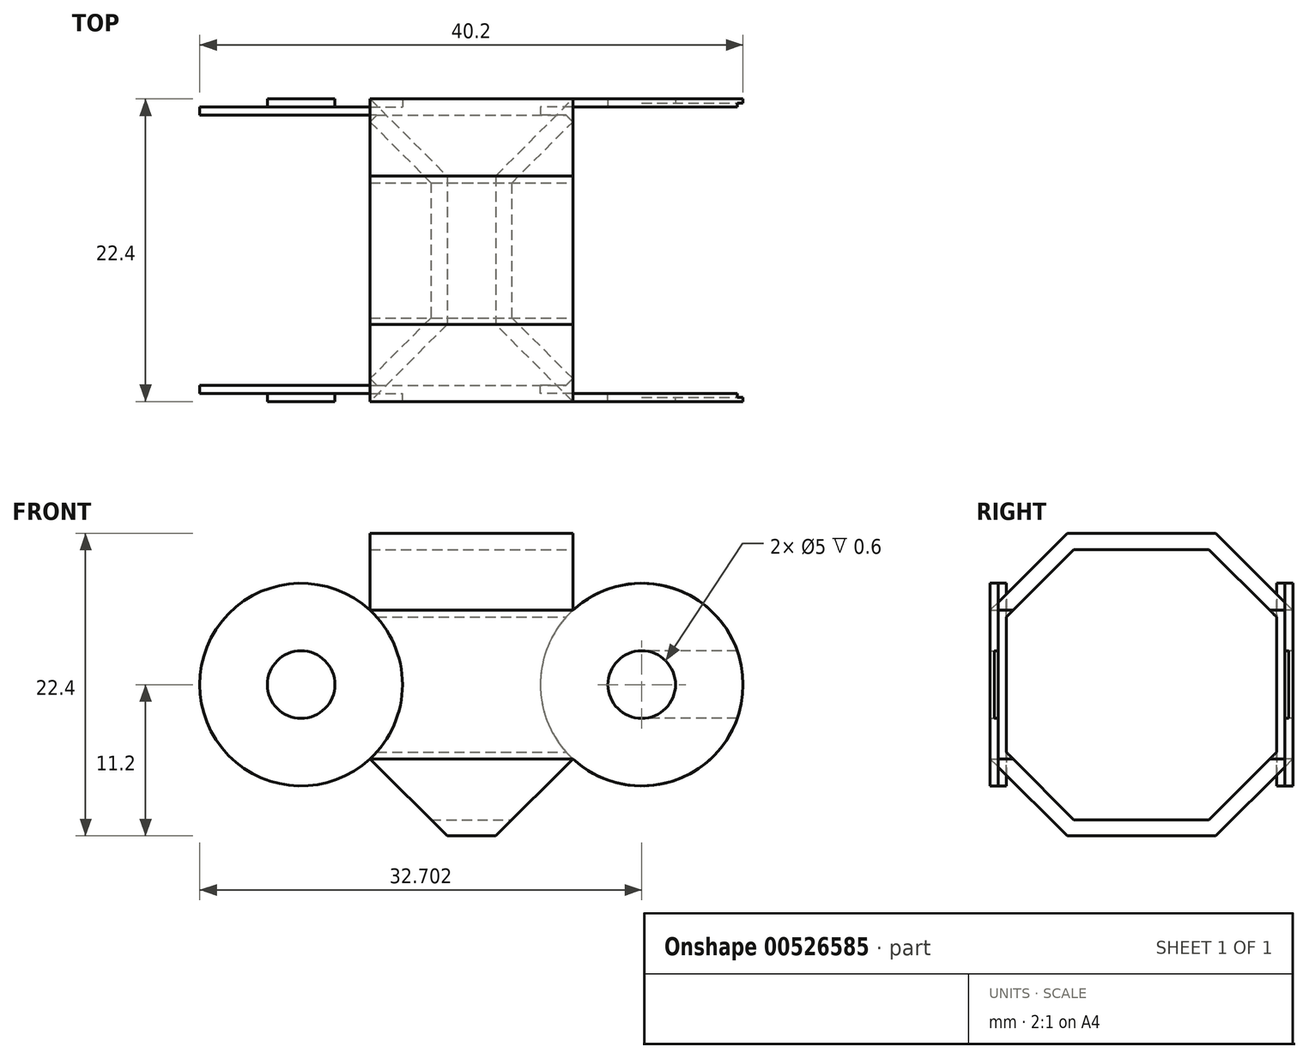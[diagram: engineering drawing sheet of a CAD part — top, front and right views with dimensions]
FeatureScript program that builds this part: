
annotation { "Feature Type Name" : "Feature", "Feature Type Description" : "" }
export const myFeature = defineFeature(function(context is Context, id is Id, definition is map)
    precondition{}
    {
        {
            var Q0;
            Q0=qCreatedBy(makeId("Right.planeOp"),FACE);
            var sketch = newSketch(context, id + "F0", { "sketchPlane" : qUnion([Q0])});
            skLineSegment(sketch, "E0", {"start": v(0, 10) * mm, "end": v(-5, 10) * mm});
            skLineSegment(sketch, "E1", {"start": v(-5, 10) * mm, "end": v(-10, 5) * mm});
            skLineSegment(sketch, "E2", {"start": v(-10, 5) * mm, "end": v(-10, -5) * mm});
            skLineSegment(sketch, "E3", {"start": v(-10, -5) * mm, "end": v(-5, -10) * mm});
            skLineSegment(sketch, "E4", {"start": v(-5, -10) * mm, "end": v(0, -10) * mm});
            skPoint(sketch, "E5", {"position": v(-10, 0) * mm});
            skLineSegment(sketch, "E6.0", {"start": v(-5.5, -11.2) * mm, "end": v(0, -11.2) * mm});
            skLineSegment(sketch, "E6.1", {"start": v(0, 11.2) * mm, "end": v(-5.5, 11.2) * mm});
            skLineSegment(sketch, "E6.2", {"start": v(-5.5, 11.2) * mm, "end": v(-11.2, 5.5) * mm});
            skLineSegment(sketch, "E6.3", {"start": v(-11.2, 5.5) * mm, "end": v(-11.2, -5.5) * mm});
            skLineSegment(sketch, "E6.4", {"start": v(-11.2, -5.5) * mm, "end": v(-5.5, -11.2) * mm});
            skLineSegment(sketch, "E7", {"start": v(0, 11.2) * mm, "end": v(0, 10) * mm});
            skLineSegment(sketch, "E8", {"start": v(0, -10) * mm, "end": v(0, -11.2) * mm});
            skSolve(sketch);
        }
        {
            var Q0;
            Q0=qSketchRegion(id+"F0",true);
            extrude(context, id + "F1", {"entities" : qUnion([Q0]), "endBound" : BoundingType.SYMMETRIC, "oppositeDirection" : true, "depth" : 15 * mm, "offsetDistance" : 25 * mm});
        }
        {
            var Q0;
            Q0=qCreatedBy(makeId("Front.planeOp"),FACE);
            var sketch = newSketch(context, id + "F2", { "sketchPlane" : qUnion([Q0])});
            skCircle(sketch, "E9", {"center": v(-12.6, 0) * mm, "radius": 7.5 * mm});
            skCircle(sketch, "E10", {"center": v(12.6, 0) * mm, "radius": 7.5 * mm});
            skCircle(sketch, "E11", {"center": v(-12.6, 0) * mm, "radius": 2.5 * mm});
            skCircle(sketch, "E12", {"center": v(12.6, 0) * mm, "radius": 2.5 * mm});
            skLineSegment(sketch, "E13", {"start": v(12.6, 2.5) * mm, "end": v(19.67, 2.5) * mm});
            skLineSegment(sketch, "E14", {"start": v(12.6, -2.5) * mm, "end": v(19.67, -2.5) * mm});
            skSolve(sketch);
        }
        {
            var Q0;
            Q0=makeQuery(id+"F2.imprint","IMPRINT",FACE,{"disambiguationData":[TD([[makeQuery(id+"F2.imprint","IMPRINT",EDGE,{"derivedFrom":sQuery(id+"F2.wireOp",EDGE,"E9")}),1.0]])]});
            var Q1;
            {var subQ0=sQuery(id+"F2.wireOp",EDGE,"E13");Q1=makeQuery(id+"F2.imprint","IMPRINT",FACE,{"disambiguationData":[TD([[makeQuery(id+"F2.imprint","IMPRINT",EDGE,{"derivedFrom":subQ0}),1.0]])]});}
            extrude(context, id + "F3", {"entities" : qUnion([Q0, Q1]), "operationType" : NewBodyOperationType.REMOVE, "depth" : 11.2 * mm, "offsetDistance" : 25 * mm});
        }
        {
            var Q0;
            {var subQ0=sQuery(id+"F2.wireOp",EDGE,"E13");Q0=makeQuery(id+"F2.imprint","IMPRINT",FACE,{"disambiguationData":[TD([[makeQuery(id+"F2.imprint","IMPRINT",EDGE,{"derivedFrom":subQ0}),1.0]])]});}
            var Q1;
            {var subQ0=sQuery(id+"F2.wireOp",EDGE,"E13");Q1=makeQuery(id+"F2.imprint","IMPRINT",FACE,{"disambiguationData":[TD([[makeQuery(id+"F2.imprint","IMPRINT",EDGE,{"derivedFrom":subQ0}),-1.0]])]});}
            extrude(context, id + "F4", {"entities" : qUnion([Q0, Q1]), "operationType" : NewBodyOperationType.ADD, "depth" : 11.2 * mm, "offsetDistance" : 25 * mm});
        }
        {
            var Q0;
            {var subQ0=sQuery(id+"F2.wireOp",EDGE,"E13");Q0=makeQuery(id+"F2.imprint","IMPRINT",FACE,{"disambiguationData":[TD([[makeQuery(id+"F2.imprint","IMPRINT",EDGE,{"derivedFrom":subQ0}),1.0]])]});}
            var Q1;
            {var subQ0=sQuery(id+"F2.wireOp",EDGE,"E13");Q1=makeQuery(id+"F2.imprint","IMPRINT",FACE,{"disambiguationData":[TD([[makeQuery(id+"F2.imprint","IMPRINT",EDGE,{"derivedFrom":subQ0}),-1.0]])]});}
            var Q2;
            {var subQ0=sQuery(id+"F2.wireOp",EDGE,"E12");var subQ1=makeQuery(id+"F2.imprint","INTERSECT",VERTEX,{"derivedFrom":[subQ0,sQuery(id+"F2.wireOp",EDGE,"E13")]});Q2=makeQuery(id+"F2.imprint","IMPRINT",FACE,{"disambiguationData":[TD([[makeQuery(id+"F2.imprint","IMPRINT",EDGE,{"disambiguationData":[TD([[subQ1,-1.0]])],"derivedFrom":subQ0}),1.0]])]});}
            extrude(context, id + "F5", {"entities" : qUnion([Q0, Q1, Q2]), "operationType" : NewBodyOperationType.REMOVE, "depth" : 10.6 * mm, "offsetDistance" : 25 * mm});
        }
        {
            var Q0;
            {var subQ0=sQuery(id+"F2.wireOp",EDGE,"E12");var subQ1=makeQuery(id+"F2.imprint","INTERSECT",VERTEX,{"derivedFrom":[subQ0,sQuery(id+"F2.wireOp",EDGE,"E13")]});Q0=makeQuery(id+"F2.imprint","IMPRINT",FACE,{"disambiguationData":[TD([[makeQuery(id+"F2.imprint","IMPRINT",EDGE,{"disambiguationData":[TD([[subQ1,-1.0]])],"derivedFrom":subQ0}),1.0]])]});}
            var Q1;
            {var subQ0=sQuery(id+"F2.wireOp",EDGE,"E13");Q1=makeQuery(id+"F2.imprint","IMPRINT",FACE,{"disambiguationData":[TD([[makeQuery(id+"F2.imprint","IMPRINT",EDGE,{"derivedFrom":subQ0}),-1.0]])]});}
            extrude(context, id + "F6", {"entities" : qUnion([Q0, Q1]), "operationType" : NewBodyOperationType.REMOVE, "depth" : 10.9 * mm, "offsetDistance" : 25 * mm});
        }
        {
            var Q0;
            Q0=makeQuery(id+"F2.imprint","IMPRINT",FACE,{"disambiguationData":[TD([[makeQuery(id+"F2.imprint","IMPRINT",EDGE,{"derivedFrom":sQuery(id+"F2.wireOp",EDGE,"E9")}),1.0]])]});
            extrude(context, id + "F7", {"entities" : qUnion([Q0]), "operationType" : NewBodyOperationType.ADD, "depth" : 10.6 * mm, "offsetDistance" : 25 * mm});
        }
        {
            var Q0;
            Q0=makeQuery(id+"F2.imprint","IMPRINT",FACE,{"disambiguationData":[TD([[makeQuery(id+"F2.imprint","IMPRINT",EDGE,{"derivedFrom":sQuery(id+"F2.wireOp",EDGE,"E11")}),1.0]])]});
            extrude(context, id + "F8", {"entities" : qUnion([Q0]), "operationType" : NewBodyOperationType.ADD, "depth" : 11.2 * mm, "offsetDistance" : 25 * mm});
        }
        {
            var Q0;
            Q0=makeQuery(id+"F2.imprint","IMPRINT",FACE,{"disambiguationData":[TD([[makeQuery(id+"F2.imprint","IMPRINT",EDGE,{"derivedFrom":sQuery(id+"F2.wireOp",EDGE,"E9")}),1.0]])]});
            var Q1;
            Q1=makeQuery(id+"F2.imprint","IMPRINT",FACE,{"disambiguationData":[TD([[makeQuery(id+"F2.imprint","IMPRINT",EDGE,{"derivedFrom":sQuery(id+"F2.wireOp",EDGE,"E11")}),1.0]])]});
            extrude(context, id + "F9", {"entities" : qUnion([Q0, Q1]), "operationType" : NewBodyOperationType.REMOVE, "depth" : 10 * mm, "offsetDistance" : 25 * mm});
        }
        {
            var Q0;
            Q0=makeQuery(id+"F1.opExtrude","SWEPT_BODY",BODY,{"disambiguationData":[OSD([sQuery(id+"F0.wireOp",EDGE,"E0"),sQuery(id+"F0.wireOp",EDGE,"E1"),sQuery(id+"F0.wireOp",EDGE,"E2"),sQuery(id+"F0.wireOp",EDGE,"E3"),sQuery(id+"F0.wireOp",EDGE,"E4"),sQuery(id+"F0.wireOp",EDGE,"E6.0"),sQuery(id+"F0.wireOp",EDGE,"E6.1"),sQuery(id+"F0.wireOp",EDGE,"E6.2"),sQuery(id+"F0.wireOp",EDGE,"E6.3"),sQuery(id+"F0.wireOp",EDGE,"E6.4"),sQuery(id+"F0.wireOp",EDGE,"E7"),sQuery(id+"F0.wireOp",EDGE,"E8")])]});
            var Q1;
            Q1=qCreatedBy(makeId("Front.planeOp"),FACE);
            mirror(context, id + "F10", {"operationType" : NewBodyOperationType.ADD, "entities" : qUnion([Q0]), "mirrorPlane" : qUnion([Q1])});
        }
        {
            var Q0;
            Q0=makeQuery(id+"F4.boolean.opBoolean","MERGE",FACE,{"derivedFrom":[makeQuery(id+"F1.opExtrude","SWEPT_FACE",FACE,{"disambiguationData":[OSD([sQuery(id+"F0.wireOp",EDGE,"E6.3")])]}),makeQuery(id+"F4.opExtrude","CAP_FACE",FACE,{"disambiguationData":[OSD([sQuery(id+"F2.wireOp",EDGE,"E10"),sQuery(id+"F2.wireOp",EDGE,"E12")])],"isStart":false})]});
            var sketch = newSketch(context, id + "F11", { "sketchPlane" : qUnion([Q0])});
            skLineSegment(sketch, "E15", {"start": v(7.5, -5.5) * mm, "end": v(1.8, -11.2) * mm});
            skLineSegment(sketch, "E16", {"start": v(1.8, -11.2) * mm, "end": v(7.5, -11.2) * mm});
            skLineSegment(sketch, "E17", {"start": v(7.5, -11.2) * mm, "end": v(7.5, -5.5) * mm});
            skLineSegment(sketch, "E18", {"start": v(-7.5, -5.5) * mm, "end": v(-7.5, -11.2) * mm});
            skLineSegment(sketch, "E19", {"start": v(-7.5, -11.2) * mm, "end": v(-1.8, -11.2) * mm});
            skLineSegment(sketch, "E20", {"start": v(-1.8, -11.2) * mm, "end": v(-7.5, -5.5) * mm});
            skSolve(sketch);
        }
        {
            var Q0;
            Q0 = qSketchRegion(id + "F11", true);
            extrude(context, id + "F12", {"entities" : qUnion([Q0]), "operationType" : NewBodyOperationType.REMOVE, "oppositeDirection" : true, "depth" : 22.4 * mm, "offsetDistance" : 25 * mm});
        }
    });
